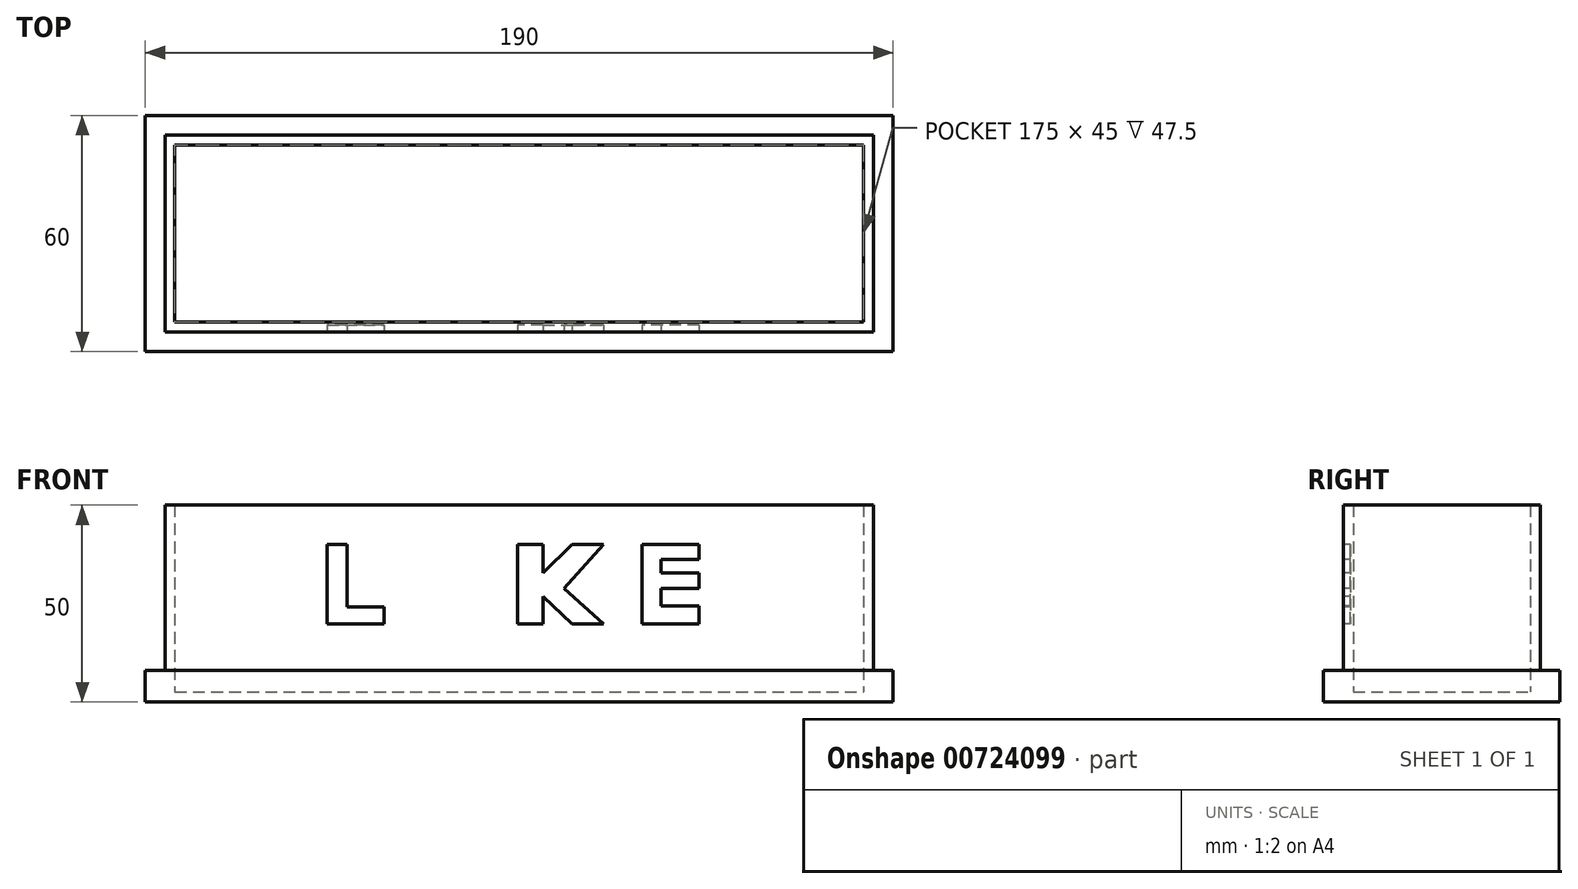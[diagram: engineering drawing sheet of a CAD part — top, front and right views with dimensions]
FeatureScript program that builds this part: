
annotation { "Feature Type Name" : "Feature", "Feature Type Description" : "" }
export const myFeature = defineFeature(function(context is Context, id is Id, definition is map)
    precondition{}
    {
        {
            var Q0;
            Q0=qCreatedBy(makeId("Top.planeOp"),FACE);
            var sketch = newSketch(context, id + "F0", { "sketchPlane" : qUnion([Q0])});
            skLineSegment(sketch, "E0", {"start": v(-47.9, 33.44) * mm, "end": v(132.1, 33.44) * mm});
            skLineSegment(sketch, "E1", {"start": v(132.1, 33.44) * mm, "end": v(132.1, -16.56) * mm});
            skLineSegment(sketch, "E2", {"start": v(132.1, -16.56) * mm, "end": v(-47.9, -16.56) * mm});
            skLineSegment(sketch, "E3", {"start": v(-47.9, -16.56) * mm, "end": v(-47.9, 33.44) * mm});
            skLineSegment(sketch, "E4.0", {"start": v(137.1, -21.56) * mm, "end": v(-52.9, -21.56) * mm});
            skLineSegment(sketch, "E4.1", {"start": v(137.1, 38.44) * mm, "end": v(137.1, -21.56) * mm});
            skLineSegment(sketch, "E4.2", {"start": v(-52.9, 38.44) * mm, "end": v(137.1, 38.44) * mm});
            skLineSegment(sketch, "E4.3", {"start": v(-52.9, -21.56) * mm, "end": v(-52.9, 38.44) * mm});
            skSolve(sketch);
        }
        {
            var Q0;
            Q0=makeQuery(id+"F0.imprint","IMPRINT",FACE,{"disambiguationData":[TD([[makeQuery(id+"F0.imprint","IMPRINT",EDGE,{"derivedFrom":sQuery(id+"F0.wireOp",EDGE,"E0")}),-1.0]])]});
            extrude(context, id + "F1", {"entities" : qUnion([Q0]), "depth" : 50 * mm, "offsetDistance" : 25 * mm});
        }
        {
            var Q0;
            Q0=makeQuery(id+"F1.opExtrude","CAP_FACE",FACE,{"disambiguationData":[OSD([sQuery(id+"F0.wireOp",EDGE,"E0"),sQuery(id+"F0.wireOp",EDGE,"E1"),sQuery(id+"F0.wireOp",EDGE,"E2"),sQuery(id+"F0.wireOp",EDGE,"E3")])],"isStart":false});
            shell(context, id + "F2", {"entities" : qUnion([Q0]), "thickness" : 2.5 * mm});
        }
        {
            var Q0;
            Q0=makeQuery(id+"F0.imprint","IMPRINT",FACE,{"disambiguationData":[TD([[makeQuery(id+"F0.imprint","IMPRINT",EDGE,{"derivedFrom":sQuery(id+"F0.wireOp",EDGE,"E0")}),1.0]])]});
            extrude(context, id + "F3", {"entities" : qUnion([Q0]), "operationType" : NewBodyOperationType.ADD, "depth" : 8 * mm, "offsetDistance" : 25 * mm});
        }
        {
            var Q0;
            Q0=makeQuery(id+"F1.opExtrude","SWEPT_FACE",FACE,{"disambiguationData":[OSD([sQuery(id+"F0.wireOp",EDGE,"E2")])]});
            var sketch = newSketch(context, id + "F4", { "sketchPlane" : qUnion([Q0])});
            skLineSegment(sketch, "E5", {"start": v(-6.7, 40.03) * mm, "end": v(-6.7, 19.84) * mm});
            skLineSegment(sketch, "E6", {"start": v(-6.7, 19.84) * mm, "end": v(7.72, 19.84) * mm});
            skLineSegment(sketch, "E7", {"start": v(7.72, 19.84) * mm, "end": v(7.72, 24.17) * mm});
            skLineSegment(sketch, "E8", {"start": v(7.72, 24.17) * mm, "end": v(-1.65, 24.17) * mm});
            skLineSegment(sketch, "E9", {"start": v(-1.65, 24.17) * mm, "end": v(-1.65, 40.03) * mm});
            skLineSegment(sketch, "E10", {"start": v(-1.65, 40.03) * mm, "end": v(-6.7, 40.03) * mm});
            skLineSegment(sketch, "E11", {"start": v(18.78, 39.35) * mm, "end": v(18.78, 27.27) * mm});
            skLineSegment(sketch, "E12", {"start": v(18.78, 27.27) * mm, "end": v(18.78, 39.35) * mm});
            skLineSegment(sketch, "E13", {"start": v(27.67, 39.5) * mm, "end": v(27.67, 27.27) * mm});
            skLineSegment(sketch, "E14", {"start": v(27.67, 27.27) * mm, "end": v(27.67, 39.5) * mm});
            skLineSegment(sketch, "E15", {"start": v(32.33, 39.5) * mm, "end": v(32.33, 27.27) * mm});
            skArc(sketch, "E16", {"start": v(32.33, 27.27) * mm, "mid": v(23.4, 18.33) * mm, "end": v(14.47, 27.27) * mm});
            skArc(sketch, "E17", {"start": v(18.78, 27.27) * mm, "mid": v(23.23, 22.82) * mm, "end": v(27.67, 27.27) * mm});
            skLineSegment(sketch, "E18", {"start": v(41.62, 40.03) * mm, "end": v(41.62, 19.84) * mm});
            skLineSegment(sketch, "E19", {"start": v(41.62, 19.84) * mm, "end": v(48.1, 19.84) * mm});
            skLineSegment(sketch, "E20", {"start": v(48.1, 19.84) * mm, "end": v(48.1, 26.81) * mm});
            skLineSegment(sketch, "E21", {"start": v(48.1, 26.81) * mm, "end": v(55.5, 19.84) * mm});
            skLineSegment(sketch, "E22", {"start": v(55.5, 19.84) * mm, "end": v(63.5, 19.84) * mm});
            skLineSegment(sketch, "E23", {"start": v(63.5, 19.84) * mm, "end": v(53.46, 28.9) * mm});
            skLineSegment(sketch, "E24", {"start": v(53.46, 28.9) * mm, "end": v(63.5, 40.01) * mm});
            skLineSegment(sketch, "E25", {"start": v(63.5, 40.01) * mm, "end": v(55.5, 40.01) * mm});
            skLineSegment(sketch, "E26", {"start": v(55.5, 40.01) * mm, "end": v(48.1, 32.75) * mm});
            skLineSegment(sketch, "E27", {"start": v(48.1, 32.75) * mm, "end": v(48.1, 40.03) * mm});
            skLineSegment(sketch, "E28", {"start": v(48.1, 40.03) * mm, "end": v(41.62, 40.03) * mm});
            skLineSegment(sketch, "E29", {"start": v(73.3, 40.03) * mm, "end": v(73.3, 19.84) * mm});
            skLineSegment(sketch, "E30", {"start": v(73.3, 19.84) * mm, "end": v(87.83, 19.84) * mm});
            skLineSegment(sketch, "E31", {"start": v(87.83, 19.84) * mm, "end": v(87.83, 24.38) * mm});
            skLineSegment(sketch, "E32", {"start": v(87.83, 24.38) * mm, "end": v(78.05, 24.38) * mm});
            skLineSegment(sketch, "E33", {"start": v(78.05, 24.38) * mm, "end": v(78.05, 28.9) * mm});
            skLineSegment(sketch, "E34", {"start": v(78.05, 28.9) * mm, "end": v(87.83, 28.9) * mm});
            skLineSegment(sketch, "E35", {"start": v(87.83, 28.9) * mm, "end": v(87.83, 32.75) * mm});
            skLineSegment(sketch, "E36", {"start": v(87.83, 32.75) * mm, "end": v(78.05, 32.75) * mm});
            skLineSegment(sketch, "E37", {"start": v(78.05, 32.75) * mm, "end": v(78.05, 36.16) * mm});
            skLineSegment(sketch, "E38", {"start": v(78.05, 36.16) * mm, "end": v(87.83, 36.16) * mm});
            skLineSegment(sketch, "E39", {"start": v(87.83, 36.16) * mm, "end": v(87.83, 40.03) * mm});
            skLineSegment(sketch, "E40", {"start": v(87.83, 40.03) * mm, "end": v(73.3, 40.03) * mm});
            skLineSegment(sketch, "E41", {"start": v(14.47, 27.27) * mm, "end": v(14.47, 39.35) * mm});
            skLineSegment(sketch, "E42", {"start": v(14.47, 39.35) * mm, "end": v(18.78, 39.35) * mm});
            skLineSegment(sketch, "E43", {"start": v(27.67, 39.5) * mm, "end": v(32.33, 39.5) * mm});
            skSolve(sketch);
        }
        {
            var Q0;
            Q0=makeQuery(id+"F4.imprint","IMPRINT",FACE,{"disambiguationData":[TD([[makeQuery(id+"F4.imprint","IMPRINT",EDGE,{"derivedFrom":sQuery(id+"F4.wireOp",EDGE,"E12")}),1.0]])]});
            var Q1;
            Q1=makeQuery(id+"F4.imprint","IMPRINT",FACE,{"disambiguationData":[TD([[makeQuery(id+"F4.imprint","IMPRINT",EDGE,{"derivedFrom":sQuery(id+"F4.wireOp",EDGE,"E5")}),1.0]])]});
            var Q2;
            Q2=makeQuery(id+"F4.imprint","IMPRINT",FACE,{"disambiguationData":[TD([[makeQuery(id+"F4.imprint","IMPRINT",EDGE,{"derivedFrom":sQuery(id+"F4.wireOp",EDGE,"E18")}),1.0]])]});
            var Q3;
            Q3=makeQuery(id+"F4.imprint","IMPRINT",FACE,{"disambiguationData":[TD([[makeQuery(id+"F4.imprint","IMPRINT",EDGE,{"derivedFrom":sQuery(id+"F4.wireOp",EDGE,"E29")}),1.0]])]});
            extrude(context, id + "F5", {"entities" : qUnion([Q0, Q1, Q2, Q3]), "operationType" : NewBodyOperationType.REMOVE, "oppositeDirection" : true, "depth" : 1.75 * mm, "offsetDistance" : 25 * mm});
        }
    });
